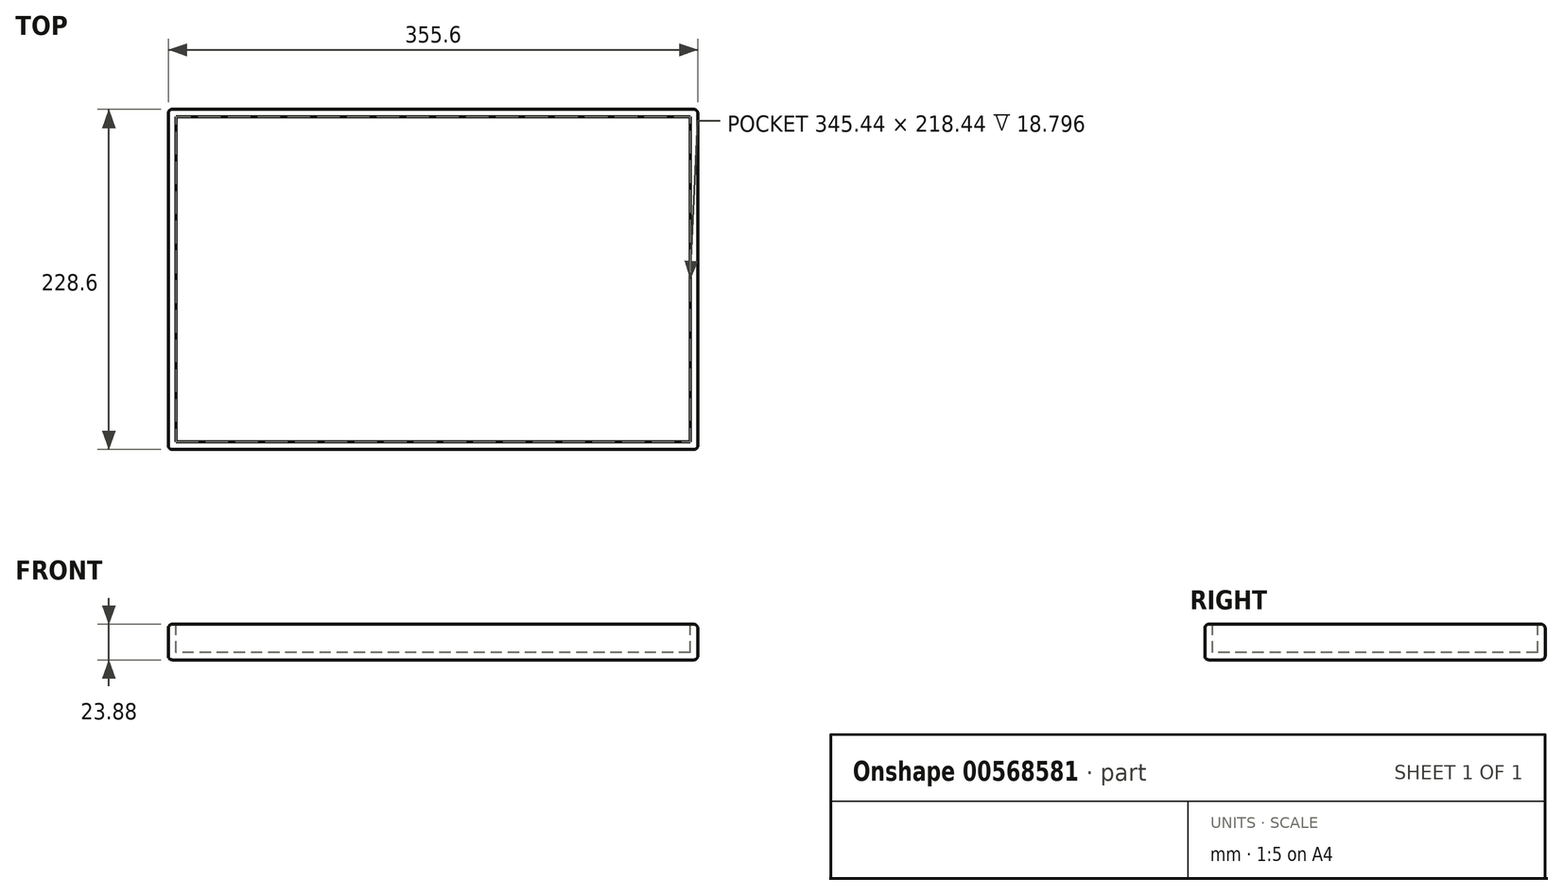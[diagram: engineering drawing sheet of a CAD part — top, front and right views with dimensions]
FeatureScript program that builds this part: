
annotation { "Feature Type Name" : "Feature", "Feature Type Description" : "" }
export const myFeature = defineFeature(function(context is Context, id is Id, definition is map)
    precondition{}
    {
        {
            var Q0;
            Q0=qCreatedBy(makeId("Top.planeOp"),FACE);
            var sketch = newSketch(context, id + "F0", { "sketchPlane" : qUnion([Q0])});
            skLineSegment(sketch, "E0.bottom", {"start": v(177.8, 114.3) * mm, "end": v(-177.8, 114.3) * mm});
            skLineSegment(sketch, "E0.top", {"start": v(177.8, -114.3) * mm, "end": v(-177.8, -114.3) * mm});
            skLineSegment(sketch, "E0.left", {"start": v(177.8, 114.3) * mm, "end": v(177.8, -114.3) * mm});
            skLineSegment(sketch, "E0.right", {"start": v(-177.8, 114.3) * mm, "end": v(-177.8, -114.3) * mm});
            skPoint(sketch, "E0.middle", {"position": v(0, 0) * mm});
            skSolve(sketch);
        }
        {
            var Q0;
            Q0 = qSketchRegion(id + "F0", true);
            extrude(context, id + "F1", {"entities" : qUnion([Q0]), "oppositeDirection" : true, "depth" : 23.88 * mm, "offsetDistance" : 25.4 * mm, "symmetric" : true});
        }
        {
            var Q0;
            Q0=makeQuery(id+"F1.opExtrude","CAP_FACE",FACE,{"disambiguationData":[OSD([sQuery(id+"F0.wireOp",EDGE,"E0.bottom"),sQuery(id+"F0.wireOp",EDGE,"E0.top"),sQuery(id+"F0.wireOp",EDGE,"E0.left"),sQuery(id+"F0.wireOp",EDGE,"E0.right")])],"isStart":true});
            shell(context, id + "F2", {"entities" : qUnion([Q0]), "thickness" : 5.08 * mm});
        }
        {
            var Q0;
            Q0=makeQuery(id+"F1.opExtrude","SWEPT_FACE",FACE,{"disambiguationData":[OSD([sQuery(id+"F0.wireOp",EDGE,"E0.right")])]});
            var Q1;
            Q1=makeQuery(id+"F1.opExtrude","SWEPT_FACE",FACE,{"disambiguationData":[OSD([sQuery(id+"F0.wireOp",EDGE,"E0.top")])]});
            var Q2;
            Q2=makeQuery(id+"F1.opExtrude","SWEPT_FACE",FACE,{"disambiguationData":[OSD([sQuery(id+"F0.wireOp",EDGE,"E0.left")])]});
            var Q3;
            Q3=makeQuery(id+"F1.opExtrude","SWEPT_FACE",FACE,{"disambiguationData":[OSD([sQuery(id+"F0.wireOp",EDGE,"E0.bottom")])]});
            fillet(context, id + "F3", {"entities" : qUnion([Q0, Q1, Q2, Q3]), "radius" : 2.54 * mm, "tangentPropagation" : true, "allowEdgeOverflow" : false});
        }
    });
